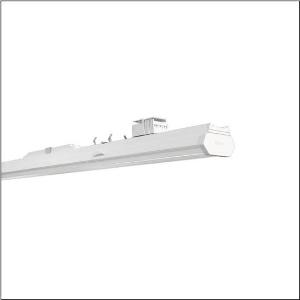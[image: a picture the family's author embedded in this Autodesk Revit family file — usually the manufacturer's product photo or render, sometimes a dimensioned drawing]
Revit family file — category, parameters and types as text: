
# Revit family: licross_r__11_protected_mo_51tp117n485g_c591
name_source: partatom
category: Lighting Fixtures
units: mm (PartAtom-declared; Revit-internal decimal feet)

## family parameters
Cut with Voids When Loaded = No
Host = Face
Light Source = No
Part Type = Normal
Room Calculation Point = No
Round Connector Dimension = Use Diameter
Shared = No

## types (1)
- Licross® 11 Protected MO (1 x LED, 8680 lm, 48.6 W, 4000K)
    Apparent Load = 49 VA
    CIE Flux Codes = 83 94 98 100 100
    Color Rendering = 80
    Color Temperature = 4000K
    Default Elevation = 1800 mm
    Description = Licross® 11 Protected MO, luminaire insert, of sheet steel, galvanised, coil coated, white, length: 1.500mm, width: 90mm, height: 101mm, LED rated luminous flux: 8.680lm, light colour: 840, control gear: ON/OFF, with plug, 3-pole, with phase selection, mains connection: 220..240V, AC, 50/60Hz, rated input power: 49W, halogen-free wiring, primary light control with lens, of plastic, primary optical cover: cover, of PMMA, light emission: direct distribution, primary light characteristic: symmetric, protection rating (complete): IP64, insulation class (complete): insulation class I (protective earthing), certification: CE, ENEC, VDE, UKCA, protection symbol: D if used in an environment with conductive dust loads with corresponding accessories, impact resistance: IK06, permissible ambient temperature for indoor applications: -25..+35°C, corresponds to IFS (International Featured Standards) requirements for safety and quality in the food industry, reducing of maximum allowable ambient temperature of 5°C with ceiling mounting, LABS conformity tested according to VDMA 24364:2018-05, packaging unit: 1 piece
    Height = 92 mm
    Lamp = 1 x LED
    Lamp Light Flux = 8680 lm
    Lamp Power = 48.6 W
    Lamp count = 1
    Length = 1500 mm
    Luminous efficacy = 179 lm/W
    Manufacturer = Siteco
    ModVariant = No
    Model = 51TP117N485G
    Mounting Place = Ceiling
    Mounting Type = Pendant
    Number of Poles = 1
    OnlyDefault = Yes
    Power Factor = 1
    Product Name = Licross® 11 Protected MO
    Product group = luminaire insert
    ProductGroupID = 901
    Protection Class = Protection class I
    Protection Degree = IP 64
    RLX_Detail_Level = 1
    RLX_Emergency_Light_Flux = 0 lm
    RLX_Emergency_Type = 0
    RLX_Emergency_Type_DB = No
    RlxData = <blob elided: 20389 chars, md5=b386e6ab>
    Socket = socket
    Standby Power = 0 W
    System Light Flux = 8680 lm
    System Power = 49 W
    Type Comments = Product without accessories
    Type Image = l_1256148.jpg
    URL = http://relux.com
    VarID = ---
    Voltage = 0 V
    Weight = 0.00 kg
    Width = 88 mm

## geometry (parser evidence)
native form markers: Blend x4, Sweep x11
no freeform markers — native parametric forms only
